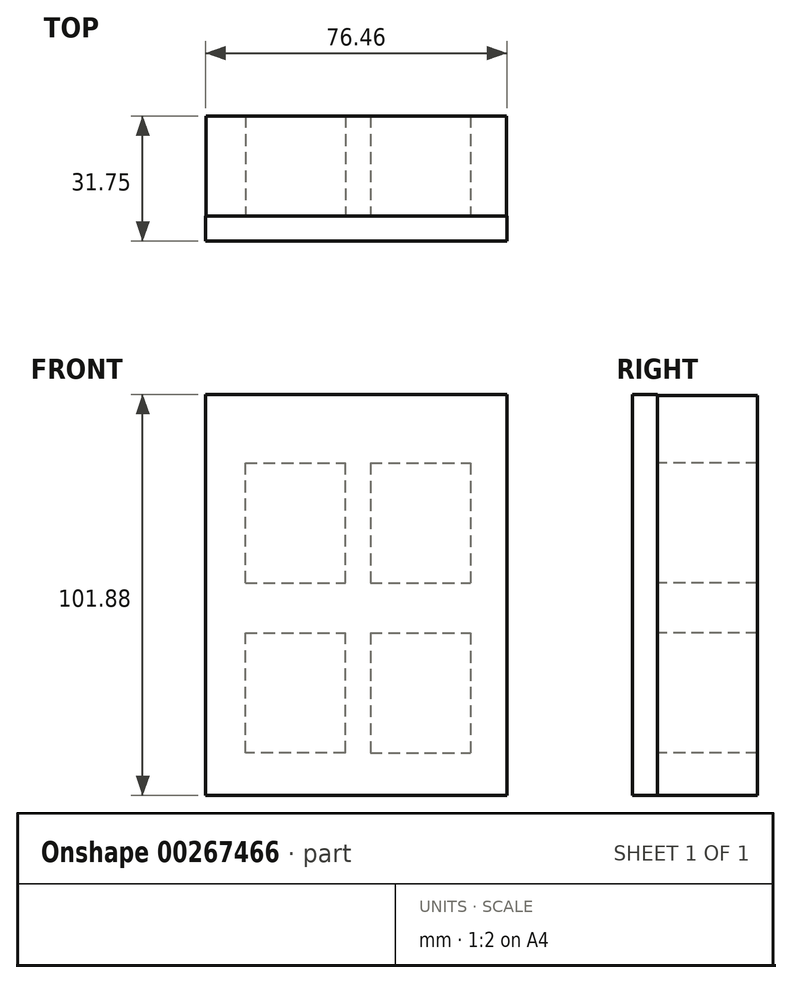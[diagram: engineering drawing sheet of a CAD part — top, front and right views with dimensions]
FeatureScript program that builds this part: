
annotation { "Feature Type Name" : "Feature", "Feature Type Description" : "" }
export const myFeature = defineFeature(function(context is Context, id is Id, definition is map)
    precondition{}
    {
        {
            var Q0;
            Q0=qCreatedBy(makeId("Front.planeOp"),FACE);
            var sketch = newSketch(context, id + "F0", { "sketchPlane" : qUnion([Q0])});
            skLineSegment(sketch, "E0.bottom", {"start": v(38.1, 50.8) * mm, "end": v(-38.1, 50.8) * mm});
            skLineSegment(sketch, "E0.top", {"start": v(38.1, -50.8) * mm, "end": v(-38.1, -50.8) * mm});
            skLineSegment(sketch, "E0.left", {"start": v(38.1, 50.8) * mm, "end": v(38.1, -50.8) * mm});
            skLineSegment(sketch, "E0.right", {"start": v(-38.1, 50.8) * mm, "end": v(-38.1, -50.8) * mm});
            skPoint(sketch, "E0.middle", {"position": v(0, 0) * mm});
            skLineSegment(sketch, "E1.bottom", {"start": v(-28.18, 3.17) * mm, "end": v(-2.78, 3.17) * mm});
            skLineSegment(sketch, "E1.top", {"start": v(-28.18, 33.65) * mm, "end": v(-2.78, 33.65) * mm});
            skLineSegment(sketch, "E1.left", {"start": v(-28.18, 3.17) * mm, "end": v(-28.18, 33.65) * mm});
            skLineSegment(sketch, "E1.right", {"start": v(-2.78, 3.17) * mm, "end": v(-2.78, 33.65) * mm});
            skLineSegment(sketch, "E2", {"start": v(-28.18, 3.17) * mm, "end": v(-28.18, -9.53) * mm});
            skLineSegment(sketch, "E3.bottom", {"start": v(-28.18, -9.53) * mm, "end": v(-2.78, -9.53) * mm});
            skLineSegment(sketch, "E3.top", {"start": v(-28.18, -9.53) * mm, "end": v(-2.78, -9.53) * mm});
            skLineSegment(sketch, "E3.left", {"start": v(-28.18, -9.53) * mm, "end": v(-28.18, -9.53) * mm});
            skLineSegment(sketch, "E3.right", {"start": v(-2.78, -9.53) * mm, "end": v(-2.78, -9.53) * mm});
            skLineSegment(sketch, "E4.bottom", {"start": v(-2.78, -40) * mm, "end": v(-28.18, -40) * mm});
            skLineSegment(sketch, "E4.top", {"start": v(-2.78, -9.53) * mm, "end": v(-28.18, -9.53) * mm});
            skLineSegment(sketch, "E4.left", {"start": v(-2.78, -40) * mm, "end": v(-2.78, -9.53) * mm});
            skLineSegment(sketch, "E4.right", {"start": v(-28.18, -40) * mm, "end": v(-28.18, -9.53) * mm});
            skLineSegment(sketch, "E5", {"start": v(-2.78, 33.65) * mm, "end": v(3.57, 33.65) * mm});
            skLineSegment(sketch, "E6.bottom", {"start": v(3.57, 33.65) * mm, "end": v(28.97, 33.65) * mm});
            skLineSegment(sketch, "E6.top", {"start": v(3.57, 3.17) * mm, "end": v(28.97, 3.17) * mm});
            skLineSegment(sketch, "E6.left", {"start": v(3.57, 33.65) * mm, "end": v(3.57, 3.17) * mm});
            skLineSegment(sketch, "E6.right", {"start": v(28.97, 33.65) * mm, "end": v(28.97, 3.17) * mm});
            skLineSegment(sketch, "E7.bottom", {"start": v(3.57, -9.51) * mm, "end": v(28.97, -9.51) * mm});
            skLineSegment(sketch, "E7.top", {"start": v(3.57, -40) * mm, "end": v(28.97, -40) * mm});
            skLineSegment(sketch, "E7.left", {"start": v(3.57, -9.51) * mm, "end": v(3.57, -40) * mm});
            skLineSegment(sketch, "E7.right", {"start": v(28.97, -9.51) * mm, "end": v(28.97, -40) * mm});
            skSolve(sketch);
        }
        {
            var Q0;
            Q0=makeQuery(id+"F0.imprint","IMPRINT",FACE,{"disambiguationData":[TD([[makeQuery(id+"F0.imprint","IMPRINT",EDGE,{"derivedFrom":sQuery(id+"F0.wireOp",EDGE,"E0.bottom")}),1.0]])]});
            extrude(context, id + "F1", {"entities" : qUnion([Q0]), "oppositeDirection" : true, "depth" : 25.4 * mm});
        }
        {
            var Q0;
            Q0=qCreatedBy(makeId("Front.planeOp"),FACE);
            var sketch = newSketch(context, id + "F2", { "sketchPlane" : qUnion([Q0])});
            skLineSegment(sketch, "E8.bottom", {"start": v(38.23, 51.04) * mm, "end": v(-38.23, 51.04) * mm});
            skLineSegment(sketch, "E8.top", {"start": v(38.23, -50.84) * mm, "end": v(-38.23, -50.84) * mm});
            skLineSegment(sketch, "E8.left", {"start": v(38.23, 51.04) * mm, "end": v(38.23, -50.84) * mm});
            skLineSegment(sketch, "E8.right", {"start": v(-38.23, 51.04) * mm, "end": v(-38.23, -50.84) * mm});
            skSolve(sketch);
        }
        {
            var Q0;
            Q0 = qSketchRegion(id + "F2", true);
            extrude(context, id + "F3", {"entities" : qUnion([Q0]), "operationType" : NewBodyOperationType.ADD, "depth" : 6.35 * mm});
        }
    });
